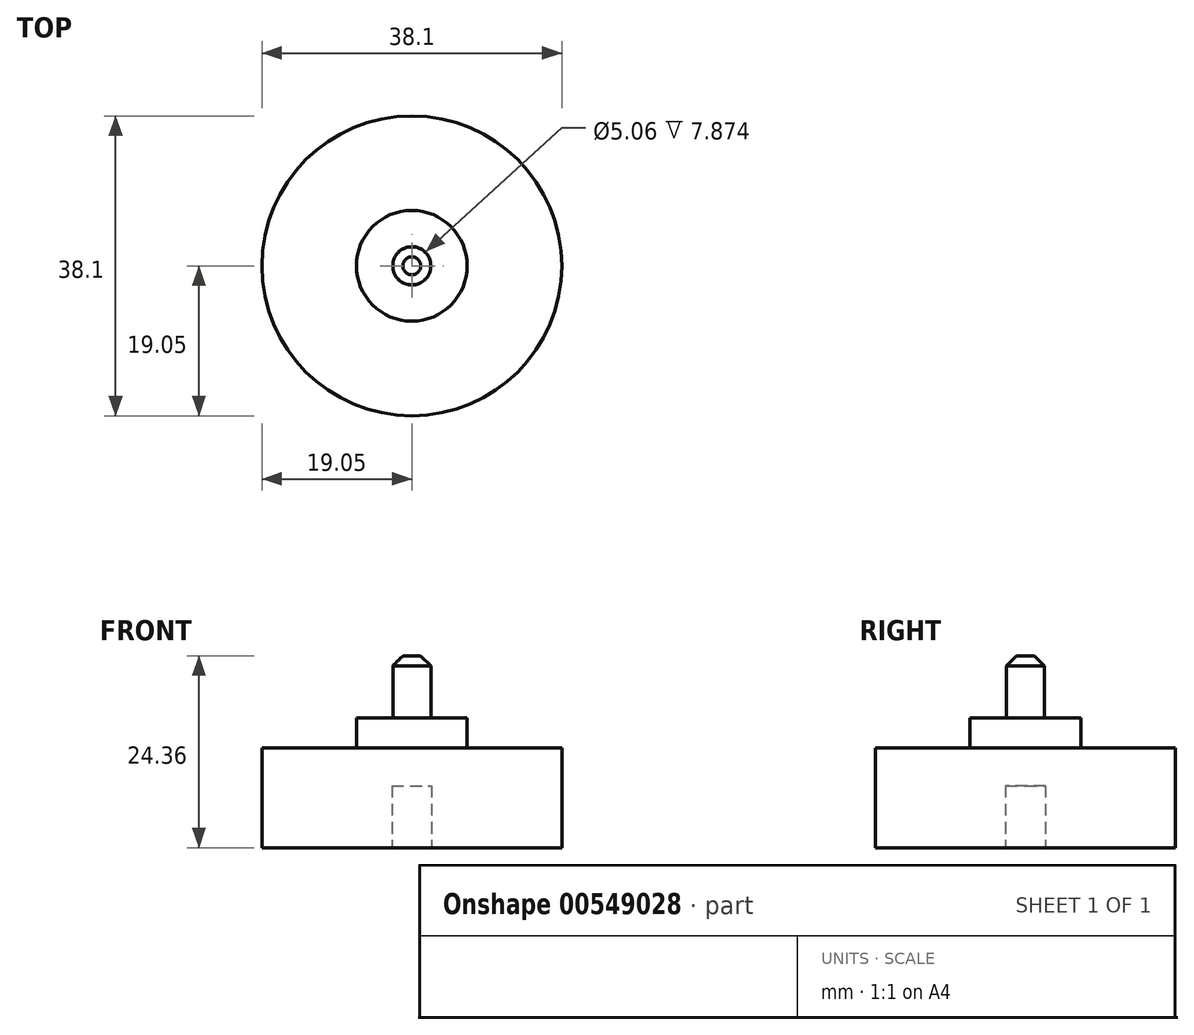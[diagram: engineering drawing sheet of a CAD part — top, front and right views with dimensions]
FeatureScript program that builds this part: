
annotation { "Feature Type Name" : "Feature", "Feature Type Description" : "" }
export const myFeature = defineFeature(function(context is Context, id is Id, definition is map)
    precondition{}
    {
        {
            var Q0;
            Q0=qCreatedBy(makeId("Front.planeOp"),FACE);
            var sketch = newSketch(context, id + "F0", { "sketchPlane" : qUnion([Q0])});
            skLineSegment(sketch, "E0", {"start": v(0, 0) * mm, "end": v(19.05, 0) * mm});
            skLineSegment(sketch, "E1", {"start": v(19.05, 0) * mm, "end": v(19.05, 12.7) * mm});
            skLineSegment(sketch, "E2", {"start": v(19.05, 12.7) * mm, "end": v(7.04, 12.7) * mm});
            skLineSegment(sketch, "E3", {"start": v(2.41, 16.51) * mm, "end": v(7.04, 16.51) * mm});
            skLineSegment(sketch, "E4", {"start": v(7.04, 16.51) * mm, "end": v(7.04, 12.7) * mm});
            skLineSegment(sketch, "E5", {"start": v(0, 24.36) * mm, "end": v(2.41, 24.36) * mm});
            skLineSegment(sketch, "E6", {"start": v(2.41, 24.36) * mm, "end": v(2.41, 16.51) * mm});
            skPoint(sketch, "E7.start.orphan", {"position": v(0, 12.7) * mm});
            skPoint(sketch, "E8.start.orphan", {"position": v(0, 16.51) * mm});
            skLineSegment(sketch, "E9", {"start": v(0, 0) * mm, "end": v(2.53, 0) * mm});
            skLineSegment(sketch, "E10", {"start": v(2.53, 0) * mm, "end": v(2.53, 7.87) * mm});
            skLineSegment(sketch, "E11", {"start": v(2.53, 7.87) * mm, "end": v(0, 7.87) * mm});
            skLineSegment(sketch, "E12", {"start": v(0, 7.87) * mm, "end": v(0, 24.36) * mm});
            skSolve(sketch);
        }
        {
            var Q0;
            Q0 = qSketchRegion(id + "F0", true);
            var Q1;
            Q1=sQuery(id+"F0.wireOp",EDGE,"E12");
            revolve(context, id + "F1", {"entities" : qUnion([Q0]), "axis" : qUnion([Q1]), "revolveType" : RevolveType.FULL});
        }
        {
            var Q0;
            Q0=makeQuery(id+"F1.opRevolve","SWEPT_EDGE",EDGE,{"disambiguationData":[OSD([sQuery(id+"F0.wireOp",EDGE,"E5"),sQuery(id+"F0.wireOp",EDGE,"E6")])]});
            chamfer(context, id + "F2", {"entities" : qUnion([Q0]), "width" : 1.27 * mm, "tangentPropagation" : true});
        }
    });
